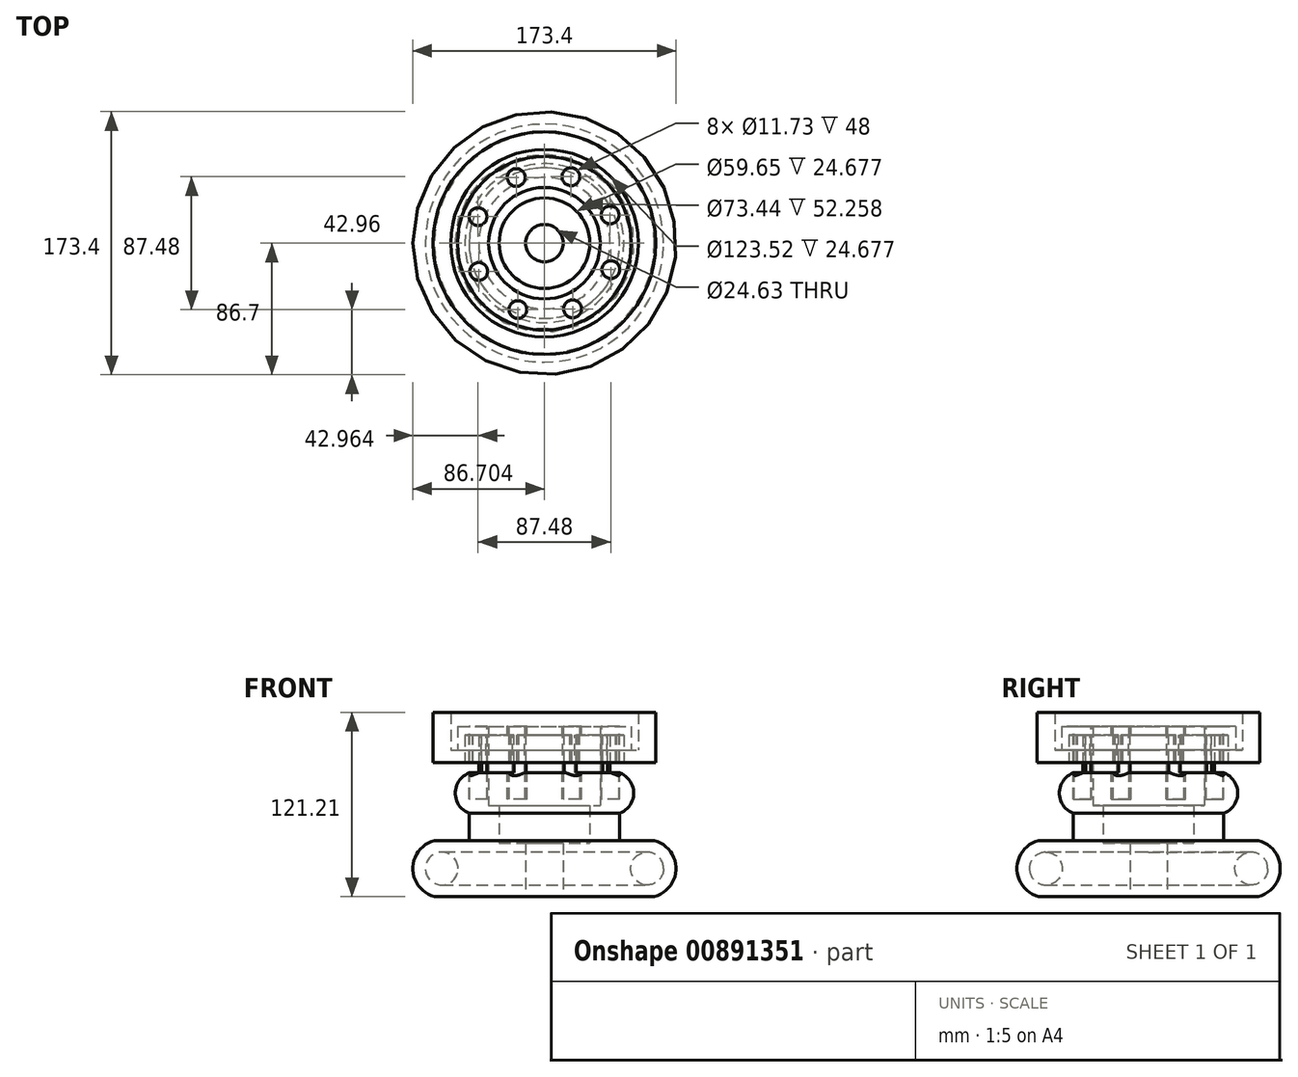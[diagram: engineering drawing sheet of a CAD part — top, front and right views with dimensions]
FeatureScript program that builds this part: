
annotation { "Feature Type Name" : "Feature", "Feature Type Description" : "" }
export const myFeature = defineFeature(function(context is Context, id is Id, definition is map)
    precondition{}
    {
        {
            var Q0;
            Q0=qCreatedBy(makeId("Front.planeOp"),FACE);
            var sketch = newSketch(context, id + "F0", { "sketchPlane" : qUnion([Q0])});
            skLineSegment(sketch, "E0", {"start": v(-3, -34.02) * mm, "end": v(-17.51, -34.02) * mm});
            skLineSegment(sketch, "E1", {"start": v(-17.51, -34.02) * mm, "end": v(-17.51, -9.34) * mm});
            skLineSegment(sketch, "E2", {"start": v(-17.51, -9.34) * mm, "end": v(-24.4, -9.34) * mm});
            skLineSegment(sketch, "E3", {"start": v(-24.4, -9.34) * mm, "end": v(-24.4, 42.91) * mm});
            skLineSegment(sketch, "E4", {"start": v(-24.4, 42.91) * mm, "end": v(-44.9, 42.91) * mm});
            skLineSegment(sketch, "E5", {"start": v(-44.9, 42.91) * mm, "end": v(-44.9, 27.3) * mm});
            skLineSegment(sketch, "E6", {"start": v(-44.9, 27.3) * mm, "end": v(-49.45, 27.3) * mm});
            skLineSegment(sketch, "E7", {"start": v(-49.45, 27.3) * mm, "end": v(-49.45, 51.99) * mm});
            skLineSegment(sketch, "E8", {"start": v(-49.45, 51.99) * mm, "end": v(-61.06, 51.99) * mm});
            skLineSegment(sketch, "E9", {"start": v(-61.06, 51.99) * mm, "end": v(-61.06, 19.14) * mm});
            skLineSegment(sketch, "E10", {"start": v(-61.06, 19.14) * mm, "end": v(-40.01, 19.14) * mm});
            skLineSegment(sketch, "E11", {"start": v(-40.01, 19.14) * mm, "end": v(-40.01, 37.1) * mm});
            skLineSegment(sketch, "E12", {"start": v(-40.01, 37.1) * mm, "end": v(-30.94, 37.1) * mm});
            skLineSegment(sketch, "E13", {"start": v(-30.94, 37.1) * mm, "end": v(-30.94, 12.25) * mm});
            skLineSegment(sketch, "E14", {"start": v(-30.94, 12.25) * mm, "end": v(-37.29, 12.25) * mm});
            skArc(sketch, "E15", {"start": v(-37.29, 12.25) * mm, "mid": v(-46.41, -1.09) * mm, "end": v(-37.29, -14.43) * mm});
            skLineSegment(sketch, "E16", {"start": v(-37.29, -14.43) * mm, "end": v(-37.29, -32.39) * mm});
            skLineSegment(sketch, "E17", {"start": v(-37.29, -32.39) * mm, "end": v(-60.15, -32.39) * mm});
            skArc(sketch, "E18", {"start": v(-60.15, -32.39) * mm, "mid": v(-74.39, -50.8) * mm, "end": v(-60.15, -69.22) * mm});
            skLineSegment(sketch, "E19", {"start": v(-60.15, -69.22) * mm, "end": v(0, -69.22) * mm});
            skLineSegment(sketch, "E20", {"start": v(0, -69.22) * mm, "end": v(0, -34.02) * mm});
            skLineSegment(sketch, "E21", {"start": v(0, -34.02) * mm, "end": v(-3, -34.02) * mm});
            skCircle(sketch, "E22", {"center": v(-55.35, -50.8) * mm, "radius": 10.8 * mm});
            skLineSegment(sketch, "E23", {"start": v(12.31, -69.22) * mm, "end": v(12.31, 3.2) * mm});
            skSolve(sketch);
        }
        {
            var Q0;
            Q0=makeQuery(id+"F0.imprint","IMPRINT",FACE,{"disambiguationData":[TD([[makeQuery(id+"F0.imprint","IMPRINT",EDGE,{"derivedFrom":sQuery(id+"F0.wireOp",EDGE,"E0")}),1.0]])]});
            var Q1;
            Q1=sQuery(id+"F0.wireOp",EDGE,"E23");
            revolve(context, id + "F1", {"surfaceOperationType" : NewSurfaceOperationType.NEW, "entities" : qUnion([Q0]), "axis" : qUnion([Q1]), "revolveType" : RevolveType.FULL});
        }
        {
            var Q0;
            Q0=makeQuery(id+"F1.opRevolve","SWEPT_FACE",FACE,{"disambiguationData":[OSD([sQuery(id+"F0.wireOp",EDGE,"E4")])]});
            var sketch = newSketch(context, id + "F2", { "sketchPlane" : qUnion([Q0])});
            skCircle(sketch, "E24", {"center": v(-30.96, -18.58) * mm, "radius": 5.86 * mm});
            skCircle(sketch, "E25.1.0", {"center": v(-5.14, -43.74) * mm, "radius": 5.86 * mm});
            skCircle(sketch, "E25.2.0", {"center": v(30.9, -43.27) * mm, "radius": 5.86 * mm});
            skCircle(sketch, "E25.3.0", {"center": v(56.05, -17.46) * mm, "radius": 5.86 * mm});
            skCircle(sketch, "E25.4.0", {"center": v(55.59, 18.58) * mm, "radius": 5.86 * mm});
            skCircle(sketch, "E25.5.0", {"center": v(29.77, 43.74) * mm, "radius": 5.86 * mm});
            skCircle(sketch, "E25.6.0", {"center": v(-6.27, 43.27) * mm, "radius": 5.86 * mm});
            skCircle(sketch, "E25.7.0", {"center": v(-31.43, 17.46) * mm, "radius": 5.86 * mm});
            skPoint(sketch, "E25.center", {"position": v(12.31, 0) * mm});
            skSolve(sketch);
        }
        {
            var Q0;
            Q0=makeQuery(id+"F2.imprint","IMPRINT",FACE,{"disambiguationData":[TD([[makeQuery(id+"F2.imprint","IMPRINT",EDGE,{"derivedFrom":sQuery(id+"F2.wireOp",EDGE,"E25.6.0")}),1.0]])]});
            var Q1;
            Q1=makeQuery(id+"F2.imprint","IMPRINT",FACE,{"disambiguationData":[TD([[makeQuery(id+"F2.imprint","IMPRINT",EDGE,{"derivedFrom":sQuery(id+"F2.wireOp",EDGE,"E25.5.0")}),1.0]])]});
            var Q2;
            Q2=makeQuery(id+"F2.imprint","IMPRINT",FACE,{"disambiguationData":[TD([[makeQuery(id+"F2.imprint","IMPRINT",EDGE,{"derivedFrom":sQuery(id+"F2.wireOp",EDGE,"E25.4.0")}),1.0]])]});
            var Q3;
            Q3=makeQuery(id+"F2.imprint","IMPRINT",FACE,{"disambiguationData":[TD([[makeQuery(id+"F2.imprint","IMPRINT",EDGE,{"derivedFrom":sQuery(id+"F2.wireOp",EDGE,"E25.3.0")}),1.0]])]});
            var Q4;
            Q4=makeQuery(id+"F2.imprint","IMPRINT",FACE,{"disambiguationData":[TD([[makeQuery(id+"F2.imprint","IMPRINT",EDGE,{"derivedFrom":sQuery(id+"F2.wireOp",EDGE,"E25.2.0")}),1.0]])]});
            var Q5;
            Q5=makeQuery(id+"F2.imprint","IMPRINT",FACE,{"disambiguationData":[TD([[makeQuery(id+"F2.imprint","IMPRINT",EDGE,{"derivedFrom":sQuery(id+"F2.wireOp",EDGE,"E25.1.0")}),1.0]])]});
            var Q6;
            Q6=makeQuery(id+"F2.imprint","IMPRINT",FACE,{"disambiguationData":[TD([[makeQuery(id+"F2.imprint","IMPRINT",EDGE,{"derivedFrom":sQuery(id+"F2.wireOp",EDGE,"E24")}),1.0]])]});
            var Q7;
            Q7=makeQuery(id+"F2.imprint","IMPRINT",FACE,{"disambiguationData":[TD([[makeQuery(id+"F2.imprint","IMPRINT",EDGE,{"derivedFrom":sQuery(id+"F2.wireOp",EDGE,"E25.7.0")}),1.0]])]});
            extrude(context, id + "F3", {"entities" : qUnion([Q0, Q1, Q2, Q3, Q4, Q5, Q6, Q7]), "operationType" : NewBodyOperationType.REMOVE, "oppositeDirection" : true, "depth" : 48 * mm, "offsetDistance" : 25 * mm});
        }
    });
